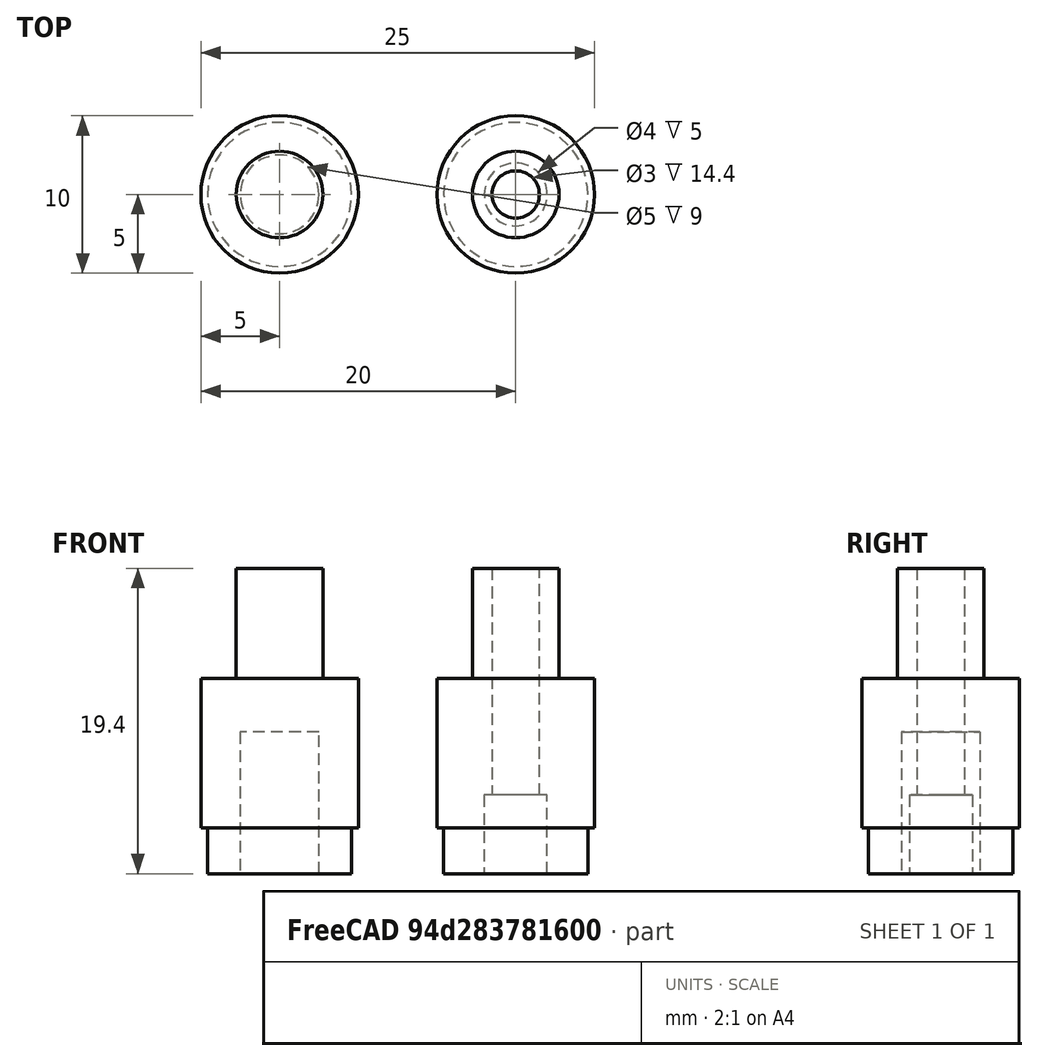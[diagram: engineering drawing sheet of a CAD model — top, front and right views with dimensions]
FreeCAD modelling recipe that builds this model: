
FCSTD DOCUMENT  (FreeCAD 0.22R38265 (Git))
Label: SBM-20-ENDS
License: All rights reserved
LicenseURL: https://en.wikipedia.org/wiki/All_rights_reserved
objects: Sketcher::SketchObject×9, TechDraw::DrawViewDimension×9, PartDesign::Pad×6, TechDraw::DrawProjGroupItem×4, TechDraw::DrawViewAnnotation×4, PartDesign::Pocket×3, PartDesign::Body×2, TechDraw::DrawProjGroup×2, TechDraw::DrawSVGTemplate×1, TechDraw::DrawPage×1
note: 48 computed .brp shape members not serialized (recipe doc carries the construction recipe); baked Part::Feature solids carry a one-line shape summary decoded from their .brp

FEATURE [Sketcher::SketchObject] Sketch
  AttachmentSupport = -> [XY_Plane]
  FullyConstrained = true
  MapMode = 5
  sketch-geometry (1):
    g0: Circle CenterX=0 CenterY=0 CenterZ=0 NormalX=0 NormalY=0 NormalZ=1 AngleXU=0 Radius=4.575
  constraints (2):
    c: Diameter(g0) = 9.15
    c: Coincident(g0,g-1)
FEATURE [PartDesign::Pad] Pad
  Direction = (0,0,1)
  Length = 2.9
  Length2 = 10
  Profile = -> Sketch
  ReferenceAxis = -> Sketch [N_Axis]
  Refine = true
  Suppressed = false
  Type = 0
FEATURE [Sketcher::SketchObject] Sketch001
  AttachmentSupport = -> [Pad]
  FullyConstrained = true
  MapMode = 5
  Placement = pos=(0,0,2.9) rot=(0,0,1;0rad)
  sketch-geometry (1):
    g0: Circle CenterX=0 CenterY=0 CenterZ=0 NormalX=0 NormalY=0 NormalZ=1 AngleXU=0 Radius=5
  constraints (2):
    c: Diameter(g0) = 10
    c: Coincident(g0,g-1)
FEATURE [PartDesign::Pad] Pad001
  BaseFeature = -> Pad
  Direction = (0,0,1)
  Length = 9.5
  Length2 = 10
  Profile = -> Sketch001
  ReferenceAxis = -> Sketch001 [N_Axis]
  Refine = true
  Suppressed = false
  Type = 0
FEATURE [Sketcher::SketchObject] Sketch002
  AttachmentSupport = -> [Pad001]
  FullyConstrained = true
  MapMode = 5
  Placement = pos=(0,0,12.4) rot=(0,0,1;0rad)
  sketch-geometry (1):
    g0: Circle CenterX=0 CenterY=0 CenterZ=0 NormalX=0 NormalY=0 NormalZ=1 AngleXU=0 Radius=2.75
  constraints (2):
    c: Diameter(g0) = 5.5
    c: Coincident(g0,g-1)
FEATURE [PartDesign::Pad] Pad002
  BaseFeature = -> Pad001
  Direction = (0,0,1)
  Length = 7
  Length2 = 10
  Profile = -> Sketch002 [Edge1]
  ReferenceAxis = -> Sketch002 [N_Axis]
  Refine = true
  Suppressed = false
  Type = 0
FEATURE [Sketcher::SketchObject] Sketch003
  AttachmentSupport = -> [Pad002]
  FullyConstrained = true
  MapMode = 5
  Placement = pos=(0,0,0) rot=(1,0,0;3.14159rad)
  sketch-geometry (1):
    g0: Circle CenterX=0 CenterY=0 CenterZ=0 NormalX=0 NormalY=0 NormalZ=1 AngleXU=0 Radius=2.5
  constraints (2):
    c: Diameter(g0) = 5
    c: Coincident(g0,g-1)
FEATURE [Sketcher::SketchObject] Sketch004
  AttachmentSupport = -> [XY_Plane001]
  FullyConstrained = true
  MapMode = 5
  sketch-geometry (1):
    g0: Circle CenterX=15 CenterY=0 CenterZ=0 NormalX=0 NormalY=0 NormalZ=1 AngleXU=0 Radius=4.575
  constraints (3):
    c: Diameter(g0) = 9.15
    c: PointOnObject(g0,g-1)
    c: DistanceX(g-1,g0) = 15
FEATURE [PartDesign::Pad] Pad003
  Direction = (0,0,1)
  Length = 2.9
  Length2 = 10
  Profile = -> Sketch004
  ReferenceAxis = -> Sketch004 [N_Axis]
  Refine = true
  Suppressed = false
  Type = 0
FEATURE [Sketcher::SketchObject] Sketch005
  AttachmentSupport = -> [Pad003]
  FullyConstrained = true
  MapMode = 5
  Placement = pos=(0,0,2.9) rot=(0,0,1;0rad)
  sketch-geometry (1):
    g0: Circle CenterX=15 CenterY=0 CenterZ=0 NormalX=0 NormalY=0 NormalZ=1 AngleXU=0 Radius=5
  constraints (3):
    c: Diameter(g0) = 10
    c: PointOnObject(g0,g-1)
    c: DistanceX(g-1,g0) = 15
FEATURE [PartDesign::Pad] Pad004
  BaseFeature = -> Pad003
  Direction = (0,0,1)
  Length = 9.5
  Length2 = 10
  Profile = -> Sketch005 [Edge1]
  ReferenceAxis = -> Sketch005 [N_Axis]
  Refine = true
  Suppressed = false
  Type = 0
FEATURE [Sketcher::SketchObject] Sketch006
  AttachmentSupport = -> [Pad004]
  FullyConstrained = true
  MapMode = 5
  Placement = pos=(0,0,12.4) rot=(0,0,1;0rad)
  sketch-geometry (1):
    g0: Circle CenterX=15 CenterY=0 CenterZ=0 NormalX=0 NormalY=0 NormalZ=1 AngleXU=0 Radius=2.75
  constraints (3):
    c: PointOnObject(g0,g-1)
    c: Diameter(g0) = 5.5
    c: DistanceX(g-1,g0) = 15
FEATURE [PartDesign::Pad] Pad005
  BaseFeature = -> Pad004
  Direction = (0,0,1)
  Length = 7
  Length2 = 10
  Profile = -> Sketch006
  ReferenceAxis = -> Sketch006 [N_Axis]
  Refine = true
  Suppressed = false
  Type = 0
FEATURE [Sketcher::SketchObject] Sketch007
  AttachmentSupport = -> [Pad005]
  FullyConstrained = true
  MapMode = 5
  Placement = pos=(0,0,0) rot=(1,0,0;3.14159rad)
  sketch-geometry (1):
    g0: Circle CenterX=15 CenterY=0 CenterZ=0 NormalX=0 NormalY=0 NormalZ=1 AngleXU=0 Radius=2
  constraints (3):
    c: Diameter(g0) = 4
    c: PointOnObject(g0,g-1)
    c: DistanceX(g-1,g0) = 15
FEATURE [PartDesign::Pocket] Pocket001
  BaseFeature = -> Pad005
  Direction = (0,0,1)
  Length = 5
  Length2 = 5
  Profile = -> Sketch007
  ReferenceAxis = -> Sketch007 [N_Axis]
  Refine = true
  Suppressed = false
  Type = 0
FEATURE [Sketcher::SketchObject] Sketch008
  AttachmentSupport = -> [Pocket001]
  FullyConstrained = true
  MapMode = 5
  Placement = pos=(0,0,5) rot=(1,0,0;3.14159rad)
  sketch-geometry (1):
    g0: Circle CenterX=15 CenterY=0 CenterZ=0 NormalX=0 NormalY=0 NormalZ=1 AngleXU=0 Radius=1.5
  constraints (3):
    c: Diameter(g0) = 3
    c: PointOnObject(g0,g-1)
    c: DistanceX(g0) = 15
FEATURE [PartDesign::Pocket] Pocket002
  BaseFeature = -> Pocket001
  Direction = (0,0,1)
  Length = 0
  Length2 = 5
  Profile = -> Sketch008 [Edge1]
  ReferenceAxis = -> Sketch008 [N_Axis]
  Refine = true
  Suppressed = false
  Type = 1
FEATURE [PartDesign::Body] Body001  label="metal-side"
  AllowCompound = false
  Group = -> [Sketch004,Pad003,Sketch005,Pad004,Sketch006,Pad005,Sketch007,Pocket001,Sketch008,Pocket002]
  Origin = -> Origin001
  Tip = -> Pocket002
FEATURE [PartDesign::Pocket] Pocket
  BaseFeature = -> Pad002
  Direction = (0,0,1)
  Length = 9
  Length2 = 5
  Profile = -> Sketch003 [Edge1]
  ReferenceAxis = -> Sketch003 [N_Axis]
  Refine = true
  Suppressed = false
  Type = 0
FEATURE [PartDesign::Body] Body  label="glass-side"
  AllowCompound = false
  Group = -> [Sketch,Pad,Sketch001,Pad001,Sketch002,Pad002,Sketch003,Pocket]
  Origin = -> Origin
  Tip = -> Pocket
FEATURE [TechDraw::DrawSVGTemplate] Template
  Height = 210
  Orientation = 1
  Template = /snap/freecad/1083/usr/share/Mod/TechDraw/Templates/A4_Landscape_TD.svg
  Width = 297
FEATURE [TechDraw::DrawProjGroupItem] View  label="Front"
  CoarseView = false
  Direction = (0,-1,0)
  Focus = 100
  HardHidden = true
  IsoCount = 0
  IsoHidden = false
  IsoVisible = false
  LockPosition = true
  Perspective = false
  Rotation = 0
  RotationVector = (1,0,0)
  Scale = 3
  ScaleType = 2
  ScrubCount = 1
  SeamHidden = false
  SeamVisible = false
  SmoothHidden = false
  SmoothVisible = true
  Source = -> [Body]
  Type = 0
  X = 0
  XDirection = (1,0,0)
  Y = 0
FEATURE [TechDraw::DrawProjGroupItem] ProjItem  label="FrontTopLeft"
  CoarseView = false
  Direction = (-0.57735,-0.57735,0.57735)
  Focus = 100
  HardHidden = true
  IsoCount = 0
  IsoHidden = false
  IsoVisible = false
  LockPosition = false
  Perspective = false
  Rotation = 0
  RotationVector = (1,0,0)
  ScaleType = 0
  ScrubCount = 1
  SeamHidden = false
  SeamVisible = false
  SmoothHidden = false
  SmoothVisible = true
  Source = -> [Body]
  Type = 6
  X = 45
  XDirection = (0.707107,-0.707107,0)
  Y = -74.2037
FEATURE [TechDraw::DrawProjGroup] ProjGroup
  Anchor = -> View
  AutoDistribute = true
  LockPosition = false
  ProjectionType = 0
  Rotation = 0
  Scale = 3
  ScaleType = 2
  Source = -> [Body]
  Views = -> [View,ProjItem]
  X = 56.4789
  Y = 166.573
  spacingX = 15
  spacingY = 15
FEATURE [TechDraw::DrawViewDimension] Dimension
  AngleOverride = false
  Arbitrary = false
  ArbitraryTolerances = false
  BoxCorners = (2) [(-15,-29.1,-1e-07),(15,29.1,1e-07)]
  EqualTolerance = true
  ExtensionAngle = 0
  FormatSpec = %.2w
  FormatSpecOverTolerance = %+.2w
  FormatSpecUnderTolerance = %+.2w
  Inverted = false
  LineAngle = 0
  LockPosition = false
  MeasureType = 1
  OverTolerance = 0
  References2D = -> [View]
  Rotation = 0
  ScaleType = 0
  TheoreticalExact = false
  Type = 0
  UnderTolerance = 0
  X = 35.063
  Y = -1.13902
FEATURE [TechDraw::DrawViewDimension] Dimension001
  AngleOverride = false
  Arbitrary = false
  ArbitraryTolerances = false
  BoxCorners = (2) [(-15,-29.1,-1e-07),(15,29.1,1e-07)]
  EqualTolerance = true
  ExtensionAngle = 0
  FormatSpec = %.2w
  FormatSpecOverTolerance = %+.2w
  FormatSpecUnderTolerance = %+.2w
  Inverted = false
  LineAngle = 0
  LockPosition = false
  MeasureType = 1
  OverTolerance = 0
  References2D = -> [View]
  Rotation = 0
  ScaleType = 0
  TheoreticalExact = false
  Type = 0
  UnderTolerance = 0
  X = 35.608
  Y = -12.4247
FEATURE [TechDraw::DrawViewDimension] Dimension002
  AngleOverride = false
  Arbitrary = false
  ArbitraryTolerances = false
  BoxCorners = (2) [(-15,-29.1,-1e-07),(15,29.1,1e-07)]
  EqualTolerance = true
  ExtensionAngle = 0
  FormatSpec = %.2w
  FormatSpecOverTolerance = %+.2w
  FormatSpecUnderTolerance = %+.2w
  Inverted = false
  LineAngle = 0
  LockPosition = false
  MeasureType = 1
  OverTolerance = 0
  References2D = -> [View]
  Rotation = 0
  ScaleType = 0
  TheoreticalExact = false
  Type = 0
  UnderTolerance = 0
  X = 33.2747
  Y = -23.3096
FEATURE [TechDraw::DrawViewDimension] Dimension003
  AngleOverride = false
  Arbitrary = false
  ArbitraryTolerances = false
  BoxCorners = (2) [(-15,-29.1,-1e-07),(15,29.1,1e-07)]
  EqualTolerance = true
  ExtensionAngle = 0
  FormatSpec = %.w
  FormatSpecOverTolerance = %+.2w
  FormatSpecUnderTolerance = %+.2w
  Inverted = false
  LineAngle = 0
  LockPosition = false
  MeasureType = 1
  OverTolerance = 0
  References2D = -> [View]
  Rotation = 0
  ScaleType = 0
  TheoreticalExact = false
  Type = 0
  UnderTolerance = 0
  X = 33.6222
  Y = 22.7951
FEATURE [TechDraw::DrawProjGroupItem] View001  label="Front001"
  CoarseView = false
  Direction = (0,-1,0)
  Focus = 100
  HardHidden = true
  IsoCount = 0
  IsoHidden = false
  IsoVisible = false
  LockPosition = true
  Perspective = false
  Rotation = 0
  RotationVector = (1,0,0)
  Scale = 3
  ScaleType = 2
  ScrubCount = 1
  SeamHidden = false
  SeamVisible = false
  SmoothHidden = false
  SmoothVisible = true
  Source = -> [Body001]
  Type = 0
  X = 0
  XDirection = (1,0,0)
  Y = 0
FEATURE [TechDraw::DrawProjGroupItem] ProjItem001  label="FrontTopLeft001"
  CoarseView = false
  Direction = (-0.57735,-0.57735,0.57735)
  Focus = 100
  HardHidden = true
  IsoCount = 0
  IsoHidden = false
  IsoVisible = false
  LockPosition = false
  Perspective = false
  Rotation = 0
  RotationVector = (1,0,0)
  ScaleType = 0
  ScrubCount = 1
  SeamHidden = false
  SeamVisible = false
  SmoothHidden = false
  SmoothVisible = true
  Source = -> [Body001]
  Type = 6
  X = 45
  XDirection = (0.707107,-0.707107,0)
  Y = -74.2037
FEATURE [TechDraw::DrawProjGroup] ProjGroup001
  Anchor = -> View001
  AutoDistribute = true
  LockPosition = false
  ProjectionType = 0
  Rotation = 0
  Scale = 3
  ScaleType = 2
  Source = -> [Body001]
  Views = -> [View001,ProjItem001]
  X = 194.691
  Y = 164.705
  spacingX = 15
  spacingY = 15
FEATURE [TechDraw::DrawViewDimension] Dimension004
  AngleOverride = false
  Arbitrary = false
  ArbitraryTolerances = false
  BoxCorners = (2) [(-15,-29.1,-1e-07),(15,29.1,1e-07)]
  EqualTolerance = true
  ExtensionAngle = 0
  FormatSpec = %.2w
  FormatSpecOverTolerance = %+.2w
  FormatSpecUnderTolerance = %+.2w
  Inverted = false
  LineAngle = 0
  LockPosition = false
  MeasureType = 1
  OverTolerance = 0
  References2D = -> [View001]
  Rotation = 0
  ScaleType = 0
  TheoreticalExact = false
  Type = 0
  UnderTolerance = 0
  X = -30.8204
  Y = -23.0334
FEATURE [TechDraw::DrawViewDimension] Dimension005
  AngleOverride = false
  Arbitrary = false
  ArbitraryTolerances = false
  BoxCorners = (2) [(-15,-29.1,-1e-07),(15,29.1,1e-07)]
  EqualTolerance = true
  ExtensionAngle = 0
  FormatSpec = %.2w
  FormatSpecOverTolerance = %+.2w
  FormatSpecUnderTolerance = %+.2w
  Inverted = false
  LineAngle = 0
  LockPosition = false
  MeasureType = 1
  OverTolerance = 0
  References2D = -> [View001]
  Rotation = 0
  ScaleType = 0
  TheoreticalExact = false
  Type = 0
  UnderTolerance = 0
  X = -33.1714
  Y = -11.9482
FEATURE [TechDraw::DrawViewDimension] Dimension006
  AngleOverride = false
  Arbitrary = false
  ArbitraryTolerances = false
  BoxCorners = (2) [(-15,-29.1,-1e-07),(15,29.1,1e-07)]
  EqualTolerance = true
  ExtensionAngle = 0
  FormatSpec = %.2w
  FormatSpecOverTolerance = %+.2w
  FormatSpecUnderTolerance = %+.2w
  Inverted = false
  LineAngle = 0
  LockPosition = false
  MeasureType = 1
  OverTolerance = 0
  References2D = -> [View001]
  Rotation = 0
  ScaleType = 0
  TheoreticalExact = false
  Type = 0
  UnderTolerance = 0
  X = 30.4792
  Y = -18.9482
FEATURE [TechDraw::DrawViewDimension] Dimension007
  AngleOverride = false
  Arbitrary = false
  ArbitraryTolerances = false
  BoxCorners = (2) [(-15,-29.1,-1e-07),(15,29.1,1e-07)]
  EqualTolerance = true
  ExtensionAngle = 0
  FormatSpec = %.2w
  FormatSpecOverTolerance = %+.2w
  FormatSpecUnderTolerance = %+.2w
  Inverted = false
  LineAngle = 0
  LockPosition = false
  MeasureType = 1
  OverTolerance = 0
  References2D = -> [View001]
  Rotation = 0
  ScaleType = 0
  TheoreticalExact = false
  Type = 0
  UnderTolerance = 0
  X = 30.0951
  Y = 1.09834
FEATURE [TechDraw::DrawViewDimension] Dimension008
  AngleOverride = false
  Arbitrary = false
  ArbitraryTolerances = false
  BoxCorners = (2) [(-15,-29.1,-1e-07),(15,29.1,1e-07)]
  EqualTolerance = true
  ExtensionAngle = 0
  FormatSpec = %.2w
  FormatSpecOverTolerance = %+.2w
  FormatSpecUnderTolerance = %+.2w
  Inverted = false
  LineAngle = 0
  LockPosition = false
  MeasureType = 1
  OverTolerance = 0
  References2D = -> [View001]
  Rotation = 0
  ScaleType = 0
  TheoreticalExact = false
  Type = 0
  UnderTolerance = 0
  X = -34.2087
  Y = 24.5186
FEATURE [TechDraw::DrawViewAnnotation] Annotation
  Font = osifont
  LineSpace = 100
  LockPosition = false
  MaxWidth = -1
  Rotation = 0
  ScaleType = 0
  Text = Glass Side
  TextSize = 5
  TextStyle = 0
  X = 57.3012
  Y = 91.0162
FEATURE [TechDraw::DrawViewAnnotation] Annotation001
  Font = osifont
  LineSpace = 100
  LockPosition = false
  MaxWidth = -1
  Rotation = 0
  ScaleType = 0
  Text = Metal Side
  TextSize = 5
  TextStyle = 0
  X = 191.971
  Y = 91.0162
FEATURE [TechDraw::DrawViewAnnotation] Annotation002
  Font = osifont
  LineSpace = 100
  LockPosition = false
  MaxWidth = -1
  Rotation = 0
  ScaleType = 0
  Text = The purpose of this design is to make your SBM-20-1 into a SBM-20
  TextSize = 3
  TextStyle = 0
  X = 79.1889
  Y = 15.9292
FEATURE [TechDraw::DrawViewAnnotation] Annotation003
  Font = osifont
  LineSpace = 100
  LockPosition = false
  MaxWidth = -1
  Rotation = 0
  ScaleType = 0
  Text = All measurements are in mm
  TextSize = 4
  TextStyle = 0
  X = 220.71
  Y = 34.4377
FEATURE [TechDraw::DrawPage] Page  label="drawing"
  KeepUpdated = true
  NextBalloonIndex = 1
  ProjectionType = 0
  Template = -> Template
  Views = -> [ProjGroup,Dimension,Dimension001,Dimension002,Dimension003,ProjGroup001,Dimension004,Dimension005,Dimension006,Dimension007,Dimension008,Annotation,Annotation001,Annotation002,Annotation003]
